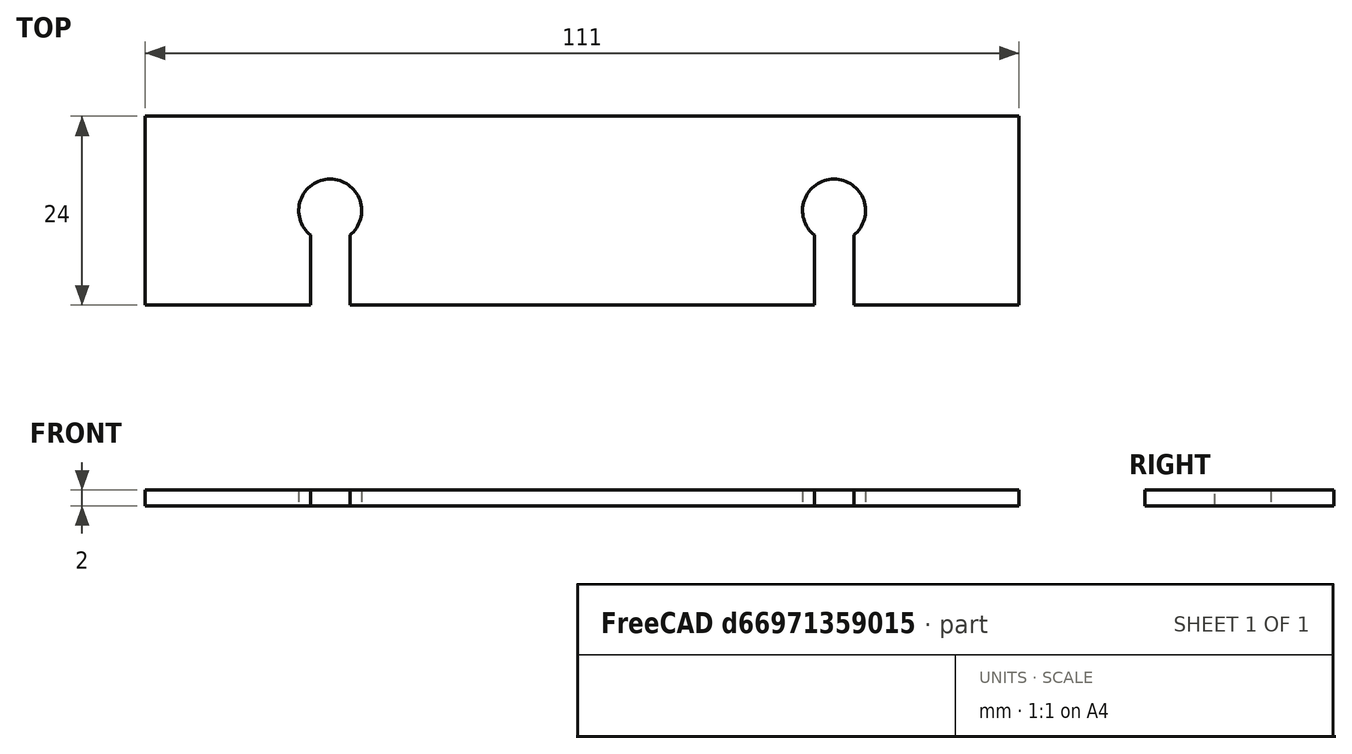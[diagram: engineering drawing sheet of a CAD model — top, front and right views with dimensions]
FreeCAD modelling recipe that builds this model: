
FCSTD DOCUMENT  (FreeCAD 0.16R6706 (Git))
Label: PS manettes part 2
License: All rights reserved
LicenseURL: http://en.wikipedia.org/wiki/All_rights_reserved
objects: Sketcher::SketchObject×1, PartDesign::Pad×1
note: 3 computed .brp shape members not serialized (recipe doc carries the construction recipe); baked Part::Feature solids carry a one-line shape summary decoded from their .brp

FEATURE [Sketcher::SketchObject] Sketch
  sketch-geometry (12):
    g0: LineSegment StartX=-55.5 StartY=20 StartZ=0 EndX=55.5 EndY=20 EndZ=0
    g1: LineSegment StartX=55.5 StartY=20 StartZ=0 EndX=55.5 EndY=-4 EndZ=0
    g2: LineSegment StartX=55.5 StartY=-4 StartZ=0 EndX=34.5 EndY=-4 EndZ=0
    g3: LineSegment StartX=-55.5 StartY=-4 StartZ=0 EndX=-55.5 EndY=20 EndZ=0
    g4: ArcOfCircle CenterX=-32 CenterY=8 CenterZ=0 NormalX=0 NormalY=0 NormalZ=1 Radius=4 StartAngle=5.38752 EndAngle=10.3204
    g5: ArcOfCircle CenterX=32 CenterY=8 CenterZ=0 NormalX=0 NormalY=0 NormalZ=1 Radius=4 StartAngle=5.38752 EndAngle=10.3204
    g6: LineSegment StartX=-29.5 StartY=4.8775 StartZ=0 EndX=-29.5 EndY=-4 EndZ=0
    g7: LineSegment StartX=-34.5 StartY=-4 StartZ=0 EndX=-34.5 EndY=4.8775 EndZ=0
    g8: LineSegment StartX=34.5 StartY=4.8775 StartZ=0 EndX=34.5 EndY=-4 EndZ=0
    g9: LineSegment StartX=29.5 StartY=-4 StartZ=0 EndX=29.5 EndY=4.8775 EndZ=0
    g10: LineSegment StartX=-34.5 StartY=-4 StartZ=0 EndX=-55.5 EndY=-4 EndZ=0
    g11: LineSegment StartX=29.5 StartY=-4 StartZ=0 EndX=-29.5 EndY=-4 EndZ=0
  constraints (36):
    c: Coincident(g0,g1)
    c: Coincident(g1,g2)
    c: Coincident(g10,g3)
    c: Coincident(g3,g0)
    c: Horizontal(g0)
    c: Horizontal(g2)
    c: Vertical(g1)
    c: Vertical(g3)
    c: DistanceX(g0,g0) = 111
    c: DistanceX(g0,g-1) = 55.5
    c: DistanceY(g1,g1) = 24
    c: DistanceY(g-1,g0) = 20
    c: DistanceX(g4,g-1) = 32
    c: Radius(g4) = 4
    c: Radius(g5) = 4
    c: DistanceX(g-1,g5) = 32
    c: DistanceY(g1,g5) = 12
    c: DistanceY(g10,g4) = 12
    c: Vertical(g6)
    c: Vertical(g7)
    c: Vertical(g8)
    c: Vertical(g9)
    c: Tangent(g2,g10)
    c: Coincident(g7,g10)
    c: Coincident(g6,g11)
    c: Coincident(g4,g6)
    c: Coincident(g4,g7)
    c: Coincident(g5,g8)
    c: Coincident(g5,g9)
    c: Coincident(g2,g8)
    c: Coincident(g11,g9)
    c: Tangent(g2,g11)
    c: DistanceX(g4,g4) = 2.5
    c: DistanceX(g4,g4) = 5
    c: DistanceX(g5,g5) = 5
    c: DistanceX(g5,g5) = 2.5
FEATURE [PartDesign::Pad] Pad
  Length = 2
  Length2 = 100
  Sketch = -> Sketch
  Type = 0
